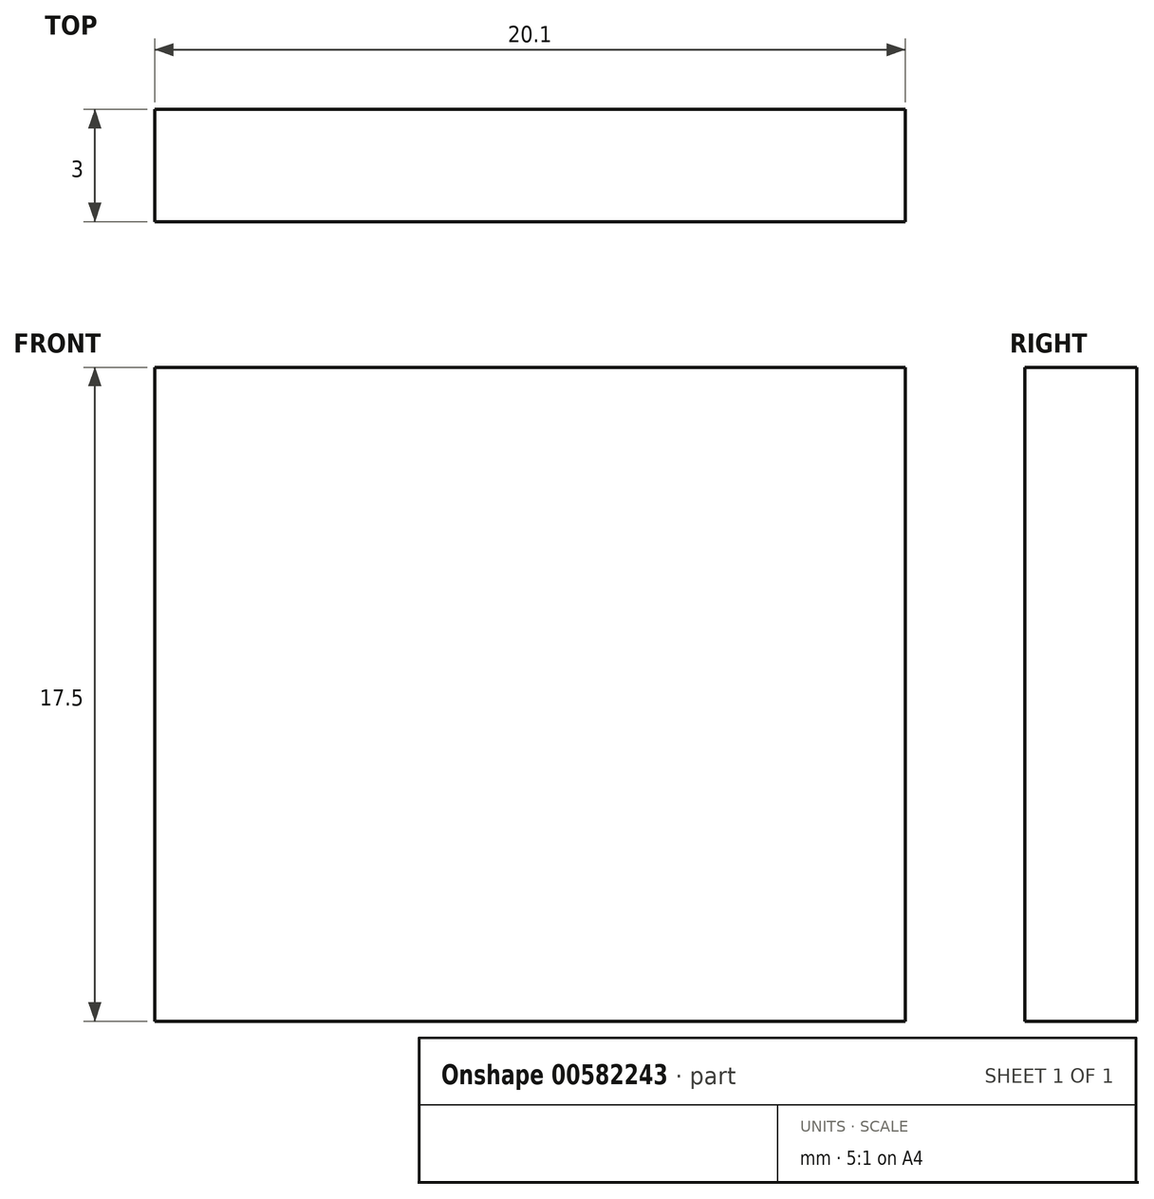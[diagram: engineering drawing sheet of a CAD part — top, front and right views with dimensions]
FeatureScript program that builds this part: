
annotation { "Feature Type Name" : "Feature", "Feature Type Description" : "" }
export const myFeature = defineFeature(function(context is Context, id is Id, definition is map)
    precondition{}
    {
        {
            var Q0;
            Q0=qCreatedBy(makeId("Front.planeOp"),FACE);
            var sketch = newSketch(context, id + "F0", { "sketchPlane" : qUnion([Q0])});
            skLineSegment(sketch, "E0.bottom", {"start": v(10.05, -8.75) * mm, "end": v(-10.05, -8.75) * mm});
            skLineSegment(sketch, "E0.top", {"start": v(10.05, 8.75) * mm, "end": v(-10.05, 8.75) * mm});
            skLineSegment(sketch, "E0.left", {"start": v(10.05, -8.75) * mm, "end": v(10.05, 8.75) * mm});
            skLineSegment(sketch, "E0.right", {"start": v(-10.05, -8.75) * mm, "end": v(-10.05, 8.75) * mm});
            skPoint(sketch, "E0.middle", {"position": v(0, 0) * mm});
            skSolve(sketch);
        }
        {
            var Q0;
            Q0 = qSketchRegion(id + "F0", true);
            extrude(context, id + "F1", {"entities" : qUnion([Q0]), "endBound" : BoundingType.SYMMETRIC, "depth" : 3 * mm, "offsetDistance" : 25 * mm});
        }
    });
